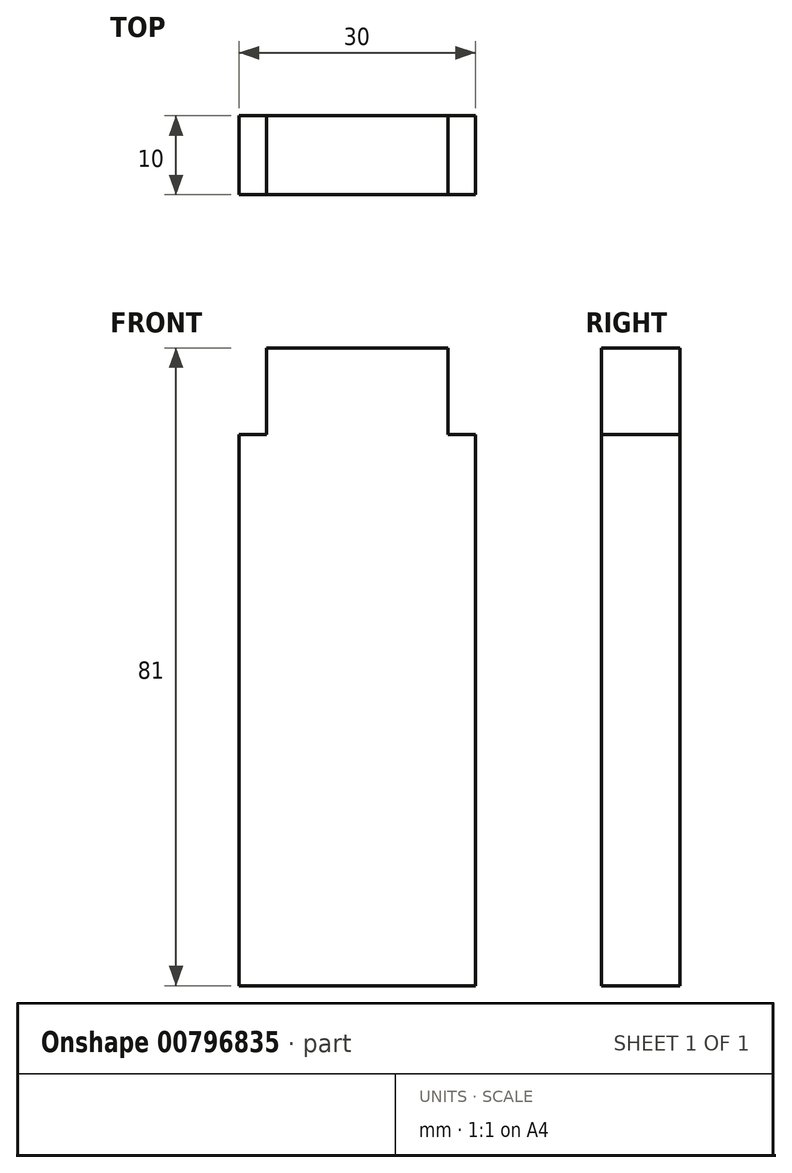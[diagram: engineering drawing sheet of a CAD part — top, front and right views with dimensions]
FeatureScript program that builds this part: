
annotation { "Feature Type Name" : "Feature", "Feature Type Description" : "" }
export const myFeature = defineFeature(function(context is Context, id is Id, definition is map)
    precondition{}
    {
        {
            var Q0;
            Q0=qCreatedBy(makeId("Top.planeOp"),FACE);
            var sketch = newSketch(context, id + "F0", { "sketchPlane" : qUnion([Q0])});
            skLineSegment(sketch, "E0.bottom", {"start": v(15, -5) * mm, "end": v(-15, -5) * mm});
            skLineSegment(sketch, "E0.top", {"start": v(15, 5) * mm, "end": v(-15, 5) * mm});
            skLineSegment(sketch, "E0.left", {"start": v(15, -5) * mm, "end": v(15, 5) * mm});
            skLineSegment(sketch, "E0.right", {"start": v(-15, -5) * mm, "end": v(-15, 5) * mm});
            skPoint(sketch, "E0.middle", {"position": v(0, 0) * mm});
            skSolve(sketch);
        }
        {
            var Q0;
            Q0=makeQuery(id+"F0.imprint","IMPRINT",FACE,{"disambiguationData":[TD([[makeQuery(id+"F0.imprint","IMPRINT",EDGE,{"derivedFrom":sQuery(id+"F0.wireOp",EDGE,"E0.bottom")}),-1.0]])]});
            extrude(context, id + "F1", {"entities" : qUnion([Q0]), "depth" : 70 * mm, "offsetDistance" : 25 * mm});
        }
        {
            var Q0;
            Q0=makeQuery(id+"F1.opExtrude","CAP_FACE",FACE,{"disambiguationData":[OSD([sQuery(id+"F0.wireOp",EDGE,"E0.bottom"),sQuery(id+"F0.wireOp",EDGE,"E0.top"),sQuery(id+"F0.wireOp",EDGE,"E0.left"),sQuery(id+"F0.wireOp",EDGE,"E0.right")])],"isStart":false});
            var sketch = newSketch(context, id + "F2", { "sketchPlane" : qUnion([Q0])});
            skLineSegment(sketch, "E1.bottom", {"start": v(11.5, -5) * mm, "end": v(-11.5, -5) * mm});
            skLineSegment(sketch, "E1.top", {"start": v(11.5, 5) * mm, "end": v(-11.5, 5) * mm});
            skLineSegment(sketch, "E1.left", {"start": v(11.5, -5) * mm, "end": v(11.5, 5) * mm});
            skLineSegment(sketch, "E1.right", {"start": v(-11.5, -5) * mm, "end": v(-11.5, 5) * mm});
            skPoint(sketch, "E1.middle", {"position": v(0, 0) * mm});
            skSolve(sketch);
        }
        {
            var Q0;
            Q0=makeQuery(id+"F2.imprint","IMPRINT",FACE,{"disambiguationData":[TD([[makeQuery(id+"F2.imprint","IMPRINT",EDGE,{"derivedFrom":sQuery(id+"F2.wireOp",EDGE,"E1.bottom")}),-1.0]])]});
            extrude(context, id + "F3", {"entities" : qUnion([Q0]), "operationType" : NewBodyOperationType.ADD, "depth" : 8 * mm, "offsetDistance" : 25 * mm});
        }
        {
            var Q0;
            Q0=makeQuery(id+"F3.opExtrude","CAP_FACE",FACE,{"disambiguationData":[OSD([sQuery(id+"F2.wireOp",EDGE,"E1.bottom"),sQuery(id+"F2.wireOp",EDGE,"E1.top"),sQuery(id+"F2.wireOp",EDGE,"E1.left"),sQuery(id+"F2.wireOp",EDGE,"E1.right")])],"isStart":false});
            var sketch = newSketch(context, id + "F4", { "sketchPlane" : qUnion([Q0])});
            skLineSegment(sketch, "E2.bottom", {"start": v(11.5, -5) * mm, "end": v(-11.5, -5) * mm});
            skLineSegment(sketch, "E2.top", {"start": v(11.5, 5) * mm, "end": v(-11.5, 5) * mm});
            skLineSegment(sketch, "E2.left", {"start": v(11.5, -5) * mm, "end": v(11.5, 5) * mm});
            skLineSegment(sketch, "E2.right", {"start": v(-11.5, -5) * mm, "end": v(-11.5, 5) * mm});
            skPoint(sketch, "E2.middle", {"position": v(0, 0) * mm});
            skSolve(sketch);
        }
        {
            var Q0;
            Q0 = qSketchRegion(id + "F4", true);
            extrude(context, id + "F5", {"entities" : qUnion([Q0]), "operationType" : NewBodyOperationType.ADD, "depth" : 3 * mm, "offsetDistance" : 25 * mm});
        }
    });
